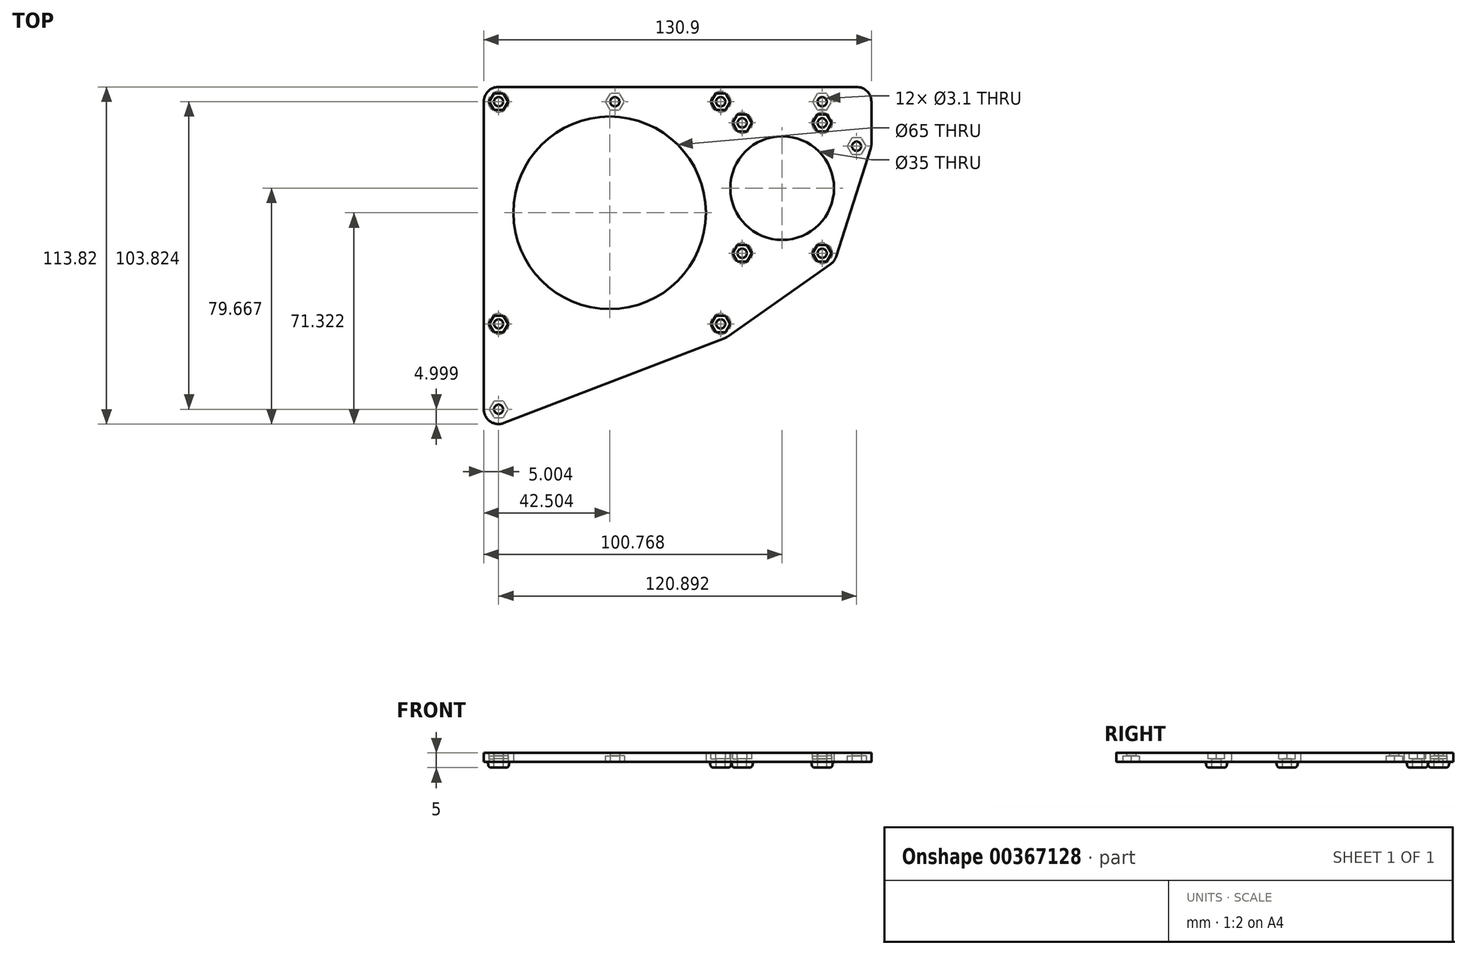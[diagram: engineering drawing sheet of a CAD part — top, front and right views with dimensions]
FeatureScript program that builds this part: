
annotation { "Feature Type Name" : "Feature", "Feature Type Description" : "" }
export const myFeature = defineFeature(function(context is Context, id is Id, definition is map)
    precondition{}
    {
        {
            var Q0;
            Q0=qCreatedBy(makeId("Top.planeOp"),FACE);
            var sketch = newSketch(context, id + "F0", { "sketchPlane" : qUnion([Q0])});
            skPoint(sketch, "E0", {"position": v(-62.97, -47.23) * mm});
            skPoint(sketch, "E1", {"position": v(-23.7, 56.6) * mm});
            skPoint(sketch, "E2", {"position": v(57.93, 41.57) * mm});
            skPoint(sketch, "E3", {"position": v(46.3, 56.6) * mm});
            skLineSegment(sketch, "E4", {"start": v(-62.97, 61.6) * mm, "end": v(57.93, 61.6) * mm});
            skLineSegment(sketch, "E5", {"start": v(62.93, 56.6) * mm, "end": v(62.93, 42.35) * mm});
            skLineSegment(sketch, "E6", {"start": v(-67.97, 56.6) * mm, "end": v(-67.97, -47.23) * mm});
            skPoint(sketch, "E7.visualSharp", {"position": v(-67.97, 61.6) * mm});
            skArc(sketch, "E7.filletArc", {"start": v(-62.97, 61.6) * mm, "mid": v(-66.5, 60.13) * mm, "end": v(-67.97, 56.6) * mm});
            skPoint(sketch, "E8.visualSharp", {"position": v(62.93, 61.6) * mm});
            skArc(sketch, "E8.filletArc", {"start": v(62.93, 56.6) * mm, "mid": v(61.46, 60.13) * mm, "end": v(57.93, 61.6) * mm});
            skLineSegment(sketch, "E9", {"start": v(-61.17, -51.9) * mm, "end": v(13.25, -23.3) * mm});
            skPoint(sketch, "E10.visualSharp", {"position": v(-67.97, -54.5) * mm});
            skArc(sketch, "E10.filletArc", {"start": v(-67.97, -47.23) * mm, "mid": v(-65.8, -51.35) * mm, "end": v(-61.17, -51.9) * mm});
            skCircle(sketch, "E11", {"center": v(-23.7, 56.6) * mm, "radius": 1.55 * mm});
            skCircle(sketch, "E12", {"center": v(46.3, 56.6) * mm, "radius": 1.55 * mm});
            skCircle(sketch, "E13", {"center": v(57.93, 41.57) * mm, "radius": 1.55 * mm});
            skCircle(sketch, "E14", {"center": v(-62.97, -47.23) * mm, "radius": 1.55 * mm});
            skPoint(sketch, "E15", {"position": v(-62.97, -18.4) * mm});
            skPoint(sketch, "E16", {"position": v(12.03, -18.4) * mm});
            skPoint(sketch, "E17", {"position": v(12.03, 56.6) * mm});
            skLineSegment(sketch, "E18", {"start": v(14.33, -22.72) * mm, "end": v(49.08, 1.7) * mm});
            skLineSegment(sketch, "E19", {"start": v(50.97, 4.26) * mm, "end": v(62.69, 40.82) * mm});
            skPoint(sketch, "E20.visualSharp", {"position": v(13.83, -23.07) * mm});
            skArc(sketch, "E20.filletArc", {"start": v(13.25, -23.3) * mm, "mid": v(13.81, -23.04) * mm, "end": v(14.33, -22.72) * mm});
            skPoint(sketch, "E21.visualSharp", {"position": v(50.45, 2.66) * mm});
            skArc(sketch, "E21.filletArc", {"start": v(49.08, 1.7) * mm, "mid": v(50.23, 2.82) * mm, "end": v(50.97, 4.26) * mm});
            skPoint(sketch, "E22.visualSharp", {"position": v(62.93, 41.57) * mm});
            skArc(sketch, "E22.filletArc", {"start": v(62.69, 40.82) * mm, "mid": v(62.87, 41.58) * mm, "end": v(62.93, 42.35) * mm});
            skCircle(sketch, "E23", {"center": v(-25.47, 19.1) * mm, "radius": 32.5 * mm});
            skCircle(sketch, "E24", {"center": v(32.8, 27.44) * mm, "radius": 17.5 * mm});
            skSolve(sketch);
        }
        {
            var Q0;
            Q0 = qSketchRegion(id + "F0", true);
            extrude(context, id + "F1", {"entities" : qUnion([Q0]), "depth" : 3 * mm});
        }
        {
            var Q0;
            Q0=makeQuery(id+"F1.opExtrude","CAP_FACE",FACE,{"disambiguationData":[OSD([sQuery(id+"F0.wireOp",EDGE,"E4"),sQuery(id+"F0.wireOp",EDGE,"E5"),sQuery(id+"F0.wireOp",EDGE,"E6"),sQuery(id+"F0.wireOp",EDGE,"E7.filletArc"),sQuery(id+"F0.wireOp",EDGE,"E8.filletArc"),sQuery(id+"F0.wireOp",EDGE,"E9"),sQuery(id+"F0.wireOp",EDGE,"E10.filletArc"),sQuery(id+"F0.wireOp",EDGE,"E11"),sQuery(id+"F0.wireOp",EDGE,"E12"),sQuery(id+"F0.wireOp",EDGE,"E13"),sQuery(id+"F0.wireOp",EDGE,"E14"),sQuery(id+"F0.wireOp",EDGE,"3iqOtTMA-anOT-yVLx-PU8o-5jLECJgI6dqX"),sQuery(id+"F0.wireOp",EDGE,"BCNSl7sb-u8Cd-CB3F-m4iC-k0AuNhckmgcP"),sQuery(id+"F0.wireOp",EDGE,"x013dWVY-SFpm-b2xf-Wu3Y-pzxELiTowayZ"),sQuery(id+"F0.wireOp",EDGE,"55sCV5fa-8bwC-iTug-WRGd-9ZglUy7d3ctR"),sQuery(id+"F0.wireOp",EDGE,"oBcL9d6C-dH0b-2MJT-6C1Z-t7KZ7XvMohC9"),sQuery(id+"F0.wireOp",EDGE,"RZnh0CVM-68zk-hnGV-QQ8E-s1oXcyv0vziq"),sQuery(id+"F0.wireOp",EDGE,"Qa9MB1tP-fu0o-2K5R-BxK5-NvYiNsFd8RXy"),sQuery(id+"F0.wireOp",EDGE,"x94zslIp-uOcx-sNJ6-LfjM-YSn8ByS7faG5"),sQuery(id+"F0.wireOp",EDGE,"E18"),sQuery(id+"F0.wireOp",EDGE,"E19"),sQuery(id+"F0.wireOp",EDGE,"E20.filletArc"),sQuery(id+"F0.wireOp",EDGE,"E21.filletArc"),sQuery(id+"F0.wireOp",EDGE,"E22.filletArc"),sQuery(id+"F0.wireOp",EDGE,"E23"),sQuery(id+"F0.wireOp",EDGE,"E24")])],"isStart":true});
            var sketch = newSketch(context, id + "F2", { "sketchPlane" : qUnion([Q0])});
            skCircle(sketch, "E25", {"center": v(-62.97, -56.6) * mm, "radius": 3.5 * mm});
            skCircle(sketch, "E26", {"center": v(12.03, -56.6) * mm, "radius": 3.5 * mm});
            skCircle(sketch, "E27", {"center": v(12.03, 18.4) * mm, "radius": 3.5 * mm});
            skCircle(sketch, "E28", {"center": v(-62.97, 18.4) * mm, "radius": 3.5 * mm});
            skCircle(sketch, "E29", {"center": v(19.3, -49.44) * mm, "radius": 3.5 * mm});
            skCircle(sketch, "E30", {"center": v(46.3, -49.44) * mm, "radius": 3.5 * mm});
            skCircle(sketch, "E31", {"center": v(46.3, -5.44) * mm, "radius": 3.5 * mm});
            skCircle(sketch, "E32", {"center": v(19.3, -5.44) * mm, "radius": 3.5 * mm});
            skSolve(sketch);
        }
        {
            var Q0;
            Q0 = qSketchRegion(id + "F2", true);
            extrude(context, id + "F3", {"entities" : qUnion([Q0]), "operationType" : NewBodyOperationType.ADD, "depth" : 2 * mm});
        }
        {
            var Q0;
            Q0=makeQuery(id+"F3.opExtrude","SWEPT_FACE",FACE,{"disambiguationData":[OSD([sQuery(id+"F2.wireOp",EDGE,"E28")])]});
            var Q1;
            Q1=makeQuery(id+"F3.opExtrude","SWEPT_FACE",FACE,{"disambiguationData":[OSD([sQuery(id+"F2.wireOp",EDGE,"E25")])]});
            var Q2;
            Q2=makeQuery(id+"F3.opExtrude","SWEPT_FACE",FACE,{"disambiguationData":[OSD([sQuery(id+"F2.wireOp",EDGE,"E27")])]});
            var Q3;
            Q3=makeQuery(id+"F3.opExtrude","SWEPT_FACE",FACE,{"disambiguationData":[OSD([sQuery(id+"F2.wireOp",EDGE,"E32")])]});
            var Q4;
            Q4=makeQuery(id+"F3.opExtrude","SWEPT_FACE",FACE,{"disambiguationData":[OSD([sQuery(id+"F2.wireOp",EDGE,"E29")])]});
            var Q5;
            Q5=makeQuery(id+"F3.opExtrude","SWEPT_FACE",FACE,{"disambiguationData":[OSD([sQuery(id+"F2.wireOp",EDGE,"E26")])]});
            var Q6;
            Q6=makeQuery(id+"F3.opExtrude","SWEPT_FACE",FACE,{"disambiguationData":[OSD([sQuery(id+"F2.wireOp",EDGE,"E31")])]});
            var Q7;
            Q7=makeQuery(id+"F3.opExtrude","SWEPT_FACE",FACE,{"disambiguationData":[OSD([sQuery(id+"F2.wireOp",EDGE,"E30")])]});
            fillet(context, id + "F4", {"entities" : qUnion([Q0, Q1, Q2, Q3, Q4, Q5, Q6, Q7]), "radius" : 1 * mm, "tangentPropagation" : true, "allowEdgeOverflow" : false});
        }
        {
            var Q0;
            Q0=makeQuery(id+"F1.opExtrude","CAP_FACE",FACE,{"disambiguationData":[OSD([sQuery(id+"F0.wireOp",EDGE,"E4"),sQuery(id+"F0.wireOp",EDGE,"E5"),sQuery(id+"F0.wireOp",EDGE,"E6"),sQuery(id+"F0.wireOp",EDGE,"E7.filletArc"),sQuery(id+"F0.wireOp",EDGE,"E8.filletArc"),sQuery(id+"F0.wireOp",EDGE,"E9"),sQuery(id+"F0.wireOp",EDGE,"E10.filletArc"),sQuery(id+"F0.wireOp",EDGE,"E11"),sQuery(id+"F0.wireOp",EDGE,"E12"),sQuery(id+"F0.wireOp",EDGE,"E13"),sQuery(id+"F0.wireOp",EDGE,"E14"),sQuery(id+"F0.wireOp",EDGE,"3iqOtTMA-anOT-yVLx-PU8o-5jLECJgI6dqX"),sQuery(id+"F0.wireOp",EDGE,"BCNSl7sb-u8Cd-CB3F-m4iC-k0AuNhckmgcP"),sQuery(id+"F0.wireOp",EDGE,"x013dWVY-SFpm-b2xf-Wu3Y-pzxELiTowayZ"),sQuery(id+"F0.wireOp",EDGE,"55sCV5fa-8bwC-iTug-WRGd-9ZglUy7d3ctR"),sQuery(id+"F0.wireOp",EDGE,"oBcL9d6C-dH0b-2MJT-6C1Z-t7KZ7XvMohC9"),sQuery(id+"F0.wireOp",EDGE,"RZnh0CVM-68zk-hnGV-QQ8E-s1oXcyv0vziq"),sQuery(id+"F0.wireOp",EDGE,"Qa9MB1tP-fu0o-2K5R-BxK5-NvYiNsFd8RXy"),sQuery(id+"F0.wireOp",EDGE,"x94zslIp-uOcx-sNJ6-LfjM-YSn8ByS7faG5"),sQuery(id+"F0.wireOp",EDGE,"E18"),sQuery(id+"F0.wireOp",EDGE,"E19"),sQuery(id+"F0.wireOp",EDGE,"E20.filletArc"),sQuery(id+"F0.wireOp",EDGE,"E21.filletArc"),sQuery(id+"F0.wireOp",EDGE,"E22.filletArc"),sQuery(id+"F0.wireOp",EDGE,"E23"),sQuery(id+"F0.wireOp",EDGE,"E24")])],"isStart":false});
            var sketch = newSketch(context, id + "F5", { "sketchPlane" : qUnion([Q0])});
            skCircle(sketch, "E33.cCircle", {"center": v(-62.97, -18.4) * mm, "radius": 2.8 * mm, "construction": true});
            skLineSegment(sketch, "E33.0", {"start": v(-61.35, -21.2) * mm, "end": v(-64.58, -21.2) * mm});
            skLineSegment(sketch, "E33.1", {"start": v(-64.58, -21.2) * mm, "end": v(-66.2, -18.4) * mm});
            skLineSegment(sketch, "E33.2", {"start": v(-66.2, -18.4) * mm, "end": v(-64.58, -15.6) * mm});
            skLineSegment(sketch, "E33.3", {"start": v(-64.58, -15.6) * mm, "end": v(-61.35, -15.6) * mm});
            skLineSegment(sketch, "E33.4", {"start": v(-61.35, -15.6) * mm, "end": v(-59.73, -18.4) * mm});
            skLineSegment(sketch, "E33.5", {"start": v(-59.73, -18.4) * mm, "end": v(-61.35, -21.2) * mm});
            skPoint(sketch, "E33.0.midPoint", {"position": v(-62.97, -21.2) * mm});
            skCircle(sketch, "E34.cCircle", {"center": v(12.03, -18.4) * mm, "radius": 2.8 * mm, "construction": true});
            skLineSegment(sketch, "E34.0", {"start": v(13.65, -21.2) * mm, "end": v(10.42, -21.2) * mm});
            skLineSegment(sketch, "E34.1", {"start": v(10.42, -21.2) * mm, "end": v(8.8, -18.4) * mm});
            skLineSegment(sketch, "E34.2", {"start": v(8.8, -18.4) * mm, "end": v(10.42, -15.6) * mm});
            skLineSegment(sketch, "E34.3", {"start": v(10.42, -15.6) * mm, "end": v(13.65, -15.6) * mm});
            skLineSegment(sketch, "E34.4", {"start": v(13.65, -15.6) * mm, "end": v(15.27, -18.4) * mm});
            skLineSegment(sketch, "E34.5", {"start": v(15.27, -18.4) * mm, "end": v(13.65, -21.2) * mm});
            skPoint(sketch, "E34.0.midPoint", {"position": v(12.03, -21.2) * mm});
            skCircle(sketch, "E35.cCircle", {"center": v(19.3, 5.44) * mm, "radius": 2.8 * mm, "construction": true});
            skLineSegment(sketch, "E35.0", {"start": v(20.91, 2.64) * mm, "end": v(17.68, 2.64) * mm});
            skLineSegment(sketch, "E35.1", {"start": v(17.68, 2.64) * mm, "end": v(16.06, 5.44) * mm});
            skLineSegment(sketch, "E35.2", {"start": v(16.06, 5.44) * mm, "end": v(17.68, 8.24) * mm});
            skLineSegment(sketch, "E35.3", {"start": v(17.68, 8.24) * mm, "end": v(20.91, 8.24) * mm});
            skLineSegment(sketch, "E35.4", {"start": v(20.91, 8.24) * mm, "end": v(22.53, 5.44) * mm});
            skLineSegment(sketch, "E35.5", {"start": v(22.53, 5.44) * mm, "end": v(20.91, 2.64) * mm});
            skPoint(sketch, "E35.0.midPoint", {"position": v(19.3, 2.64) * mm});
            skCircle(sketch, "E36.cCircle", {"center": v(-62.97, 56.6) * mm, "radius": 2.8 * mm, "construction": true});
            skLineSegment(sketch, "E36.0", {"start": v(-61.35, 53.8) * mm, "end": v(-64.58, 53.8) * mm});
            skLineSegment(sketch, "E36.1", {"start": v(-64.58, 53.8) * mm, "end": v(-66.2, 56.6) * mm});
            skLineSegment(sketch, "E36.2", {"start": v(-66.2, 56.6) * mm, "end": v(-64.58, 59.4) * mm});
            skLineSegment(sketch, "E36.3", {"start": v(-64.58, 59.4) * mm, "end": v(-61.35, 59.4) * mm});
            skLineSegment(sketch, "E36.4", {"start": v(-61.35, 59.4) * mm, "end": v(-59.73, 56.6) * mm});
            skLineSegment(sketch, "E36.5", {"start": v(-59.73, 56.6) * mm, "end": v(-61.35, 53.8) * mm});
            skPoint(sketch, "E36.0.midPoint", {"position": v(-62.97, 53.8) * mm});
            skCircle(sketch, "E37.cCircle", {"center": v(12.03, 56.6) * mm, "radius": 2.8 * mm, "construction": true});
            skLineSegment(sketch, "E37.0", {"start": v(13.65, 53.8) * mm, "end": v(10.42, 53.8) * mm});
            skLineSegment(sketch, "E37.1", {"start": v(10.42, 53.8) * mm, "end": v(8.8, 56.6) * mm});
            skLineSegment(sketch, "E37.2", {"start": v(8.8, 56.6) * mm, "end": v(10.42, 59.4) * mm});
            skLineSegment(sketch, "E37.3", {"start": v(10.42, 59.4) * mm, "end": v(13.65, 59.4) * mm});
            skLineSegment(sketch, "E37.4", {"start": v(13.65, 59.4) * mm, "end": v(15.27, 56.6) * mm});
            skLineSegment(sketch, "E37.5", {"start": v(15.27, 56.6) * mm, "end": v(13.65, 53.8) * mm});
            skPoint(sketch, "E37.0.midPoint", {"position": v(12.03, 53.8) * mm});
            skCircle(sketch, "E38.cCircle", {"center": v(19.3, 49.44) * mm, "radius": 2.8 * mm, "construction": true});
            skLineSegment(sketch, "E38.0", {"start": v(20.91, 46.64) * mm, "end": v(17.68, 46.64) * mm});
            skLineSegment(sketch, "E38.1", {"start": v(17.68, 46.64) * mm, "end": v(16.06, 49.44) * mm});
            skLineSegment(sketch, "E38.2", {"start": v(16.06, 49.44) * mm, "end": v(17.68, 52.24) * mm});
            skLineSegment(sketch, "E38.3", {"start": v(17.68, 52.24) * mm, "end": v(20.91, 52.24) * mm});
            skLineSegment(sketch, "E38.4", {"start": v(20.91, 52.24) * mm, "end": v(22.53, 49.44) * mm});
            skLineSegment(sketch, "E38.5", {"start": v(22.53, 49.44) * mm, "end": v(20.91, 46.64) * mm});
            skPoint(sketch, "E38.0.midPoint", {"position": v(19.3, 46.64) * mm});
            skCircle(sketch, "E39.cCircle", {"center": v(46.3, 49.44) * mm, "radius": 2.8 * mm, "construction": true});
            skLineSegment(sketch, "E39.0", {"start": v(47.91, 46.64) * mm, "end": v(44.68, 46.64) * mm});
            skLineSegment(sketch, "E39.1", {"start": v(44.68, 46.64) * mm, "end": v(43.06, 49.44) * mm});
            skLineSegment(sketch, "E39.2", {"start": v(43.06, 49.44) * mm, "end": v(44.68, 52.24) * mm});
            skLineSegment(sketch, "E39.3", {"start": v(44.68, 52.24) * mm, "end": v(47.91, 52.24) * mm});
            skLineSegment(sketch, "E39.4", {"start": v(47.91, 52.24) * mm, "end": v(49.53, 49.44) * mm});
            skLineSegment(sketch, "E39.5", {"start": v(49.53, 49.44) * mm, "end": v(47.91, 46.64) * mm});
            skPoint(sketch, "E39.0.midPoint", {"position": v(46.3, 46.64) * mm});
            skCircle(sketch, "E40.cCircle", {"center": v(46.3, 5.44) * mm, "radius": 2.8 * mm, "construction": true});
            skLineSegment(sketch, "E40.0", {"start": v(44.68, 8.24) * mm, "end": v(47.91, 8.24) * mm});
            skLineSegment(sketch, "E40.1", {"start": v(47.91, 8.24) * mm, "end": v(49.53, 5.44) * mm});
            skLineSegment(sketch, "E40.2", {"start": v(49.53, 5.44) * mm, "end": v(47.91, 2.64) * mm});
            skLineSegment(sketch, "E40.3", {"start": v(47.91, 2.64) * mm, "end": v(44.68, 2.64) * mm});
            skLineSegment(sketch, "E40.4", {"start": v(44.68, 2.64) * mm, "end": v(43.06, 5.44) * mm});
            skLineSegment(sketch, "E40.5", {"start": v(43.06, 5.44) * mm, "end": v(44.68, 8.24) * mm});
            skPoint(sketch, "E40.0.midPoint", {"position": v(46.3, 8.24) * mm});
            skSolve(sketch);
        }
        {
            var Q0;
            Q0 = qSketchRegion(id + "F5", true);
            extrude(context, id + "F6", {"entities" : qUnion([Q0]), "operationType" : NewBodyOperationType.REMOVE, "oppositeDirection" : true, "depth" : 2 * mm});
        }
        {
            var Q0;
            Q0=makeQuery(id+"F1.opExtrude","CAP_FACE",FACE,{"disambiguationData":[OSD([sQuery(id+"F0.wireOp",EDGE,"E4"),sQuery(id+"F0.wireOp",EDGE,"E5"),sQuery(id+"F0.wireOp",EDGE,"E6"),sQuery(id+"F0.wireOp",EDGE,"E7.filletArc"),sQuery(id+"F0.wireOp",EDGE,"E8.filletArc"),sQuery(id+"F0.wireOp",EDGE,"E9"),sQuery(id+"F0.wireOp",EDGE,"E10.filletArc"),sQuery(id+"F0.wireOp",EDGE,"E11"),sQuery(id+"F0.wireOp",EDGE,"E12"),sQuery(id+"F0.wireOp",EDGE,"E13"),sQuery(id+"F0.wireOp",EDGE,"E14"),sQuery(id+"F0.wireOp",EDGE,"E18"),sQuery(id+"F0.wireOp",EDGE,"E19"),sQuery(id+"F0.wireOp",EDGE,"E20.filletArc"),sQuery(id+"F0.wireOp",EDGE,"E21.filletArc"),sQuery(id+"F0.wireOp",EDGE,"E22.filletArc"),sQuery(id+"F0.wireOp",EDGE,"E23"),sQuery(id+"F0.wireOp",EDGE,"E24")])],"isStart":false});
            var sketch = newSketch(context, id + "F7", { "sketchPlane" : qUnion([Q0])});
            skCircle(sketch, "E41", {"center": v(-62.97, 56.6) * mm, "radius": 1.55 * mm});
            skCircle(sketch, "E42", {"center": v(-62.97, -18.4) * mm, "radius": 1.55 * mm});
            skCircle(sketch, "E43", {"center": v(19.3, 5.44) * mm, "radius": 1.55 * mm});
            skCircle(sketch, "E44", {"center": v(46.3, 5.44) * mm, "radius": 1.55 * mm});
            skCircle(sketch, "E45", {"center": v(46.3, 49.44) * mm, "radius": 1.55 * mm});
            skCircle(sketch, "E46", {"center": v(19.3, 49.44) * mm, "radius": 1.55 * mm});
            skCircle(sketch, "E47", {"center": v(12.03, -18.4) * mm, "radius": 1.55 * mm});
            skCircle(sketch, "E48", {"center": v(12.03, 56.6) * mm, "radius": 1.55 * mm});
            skSolve(sketch);
        }
        {
            var Q0;
            Q0 = qSketchRegion(id + "F7", true);
            extrude(context, id + "F8", {"entities" : qUnion([Q0]), "operationType" : NewBodyOperationType.REMOVE, "oppositeDirection" : true, "depth" : 25 * mm});
        }
        {
            var Q0;
            Q0=makeQuery(id+"F1.opExtrude","CAP_FACE",FACE,{"disambiguationData":[OSD([sQuery(id+"F0.wireOp",EDGE,"E4"),sQuery(id+"F0.wireOp",EDGE,"E5"),sQuery(id+"F0.wireOp",EDGE,"E6"),sQuery(id+"F0.wireOp",EDGE,"E7.filletArc"),sQuery(id+"F0.wireOp",EDGE,"E8.filletArc"),sQuery(id+"F0.wireOp",EDGE,"E9"),sQuery(id+"F0.wireOp",EDGE,"E10.filletArc"),sQuery(id+"F0.wireOp",EDGE,"E11"),sQuery(id+"F0.wireOp",EDGE,"E12"),sQuery(id+"F0.wireOp",EDGE,"E13"),sQuery(id+"F0.wireOp",EDGE,"E14"),sQuery(id+"F0.wireOp",EDGE,"E18"),sQuery(id+"F0.wireOp",EDGE,"E19"),sQuery(id+"F0.wireOp",EDGE,"E20.filletArc"),sQuery(id+"F0.wireOp",EDGE,"E21.filletArc"),sQuery(id+"F0.wireOp",EDGE,"E22.filletArc"),sQuery(id+"F0.wireOp",EDGE,"E23"),sQuery(id+"F0.wireOp",EDGE,"E24")])],"isStart":true});
            var sketch = newSketch(context, id + "F9", { "sketchPlane" : qUnion([Q0])});
            skCircle(sketch, "E49.cCircle", {"center": v(-62.97, 47.23) * mm, "radius": 2.8 * mm, "construction": true});
            skLineSegment(sketch, "E49.0", {"start": v(-61.35, 44.43) * mm, "end": v(-64.58, 44.43) * mm});
            skLineSegment(sketch, "E49.1", {"start": v(-64.58, 44.43) * mm, "end": v(-66.2, 47.23) * mm});
            skLineSegment(sketch, "E49.2", {"start": v(-66.2, 47.23) * mm, "end": v(-64.58, 50.03) * mm});
            skLineSegment(sketch, "E49.3", {"start": v(-64.58, 50.03) * mm, "end": v(-61.35, 50.03) * mm});
            skLineSegment(sketch, "E49.4", {"start": v(-61.35, 50.03) * mm, "end": v(-59.73, 47.23) * mm});
            skLineSegment(sketch, "E49.5", {"start": v(-59.73, 47.23) * mm, "end": v(-61.35, 44.43) * mm});
            skPoint(sketch, "E49.0.midPoint", {"position": v(-62.97, 44.43) * mm});
            skCircle(sketch, "E50.cCircle", {"center": v(-23.7, -56.6) * mm, "radius": 2.8 * mm, "construction": true});
            skLineSegment(sketch, "E50.0", {"start": v(-22.09, -59.4) * mm, "end": v(-25.32, -59.4) * mm});
            skLineSegment(sketch, "E50.1", {"start": v(-25.32, -59.4) * mm, "end": v(-26.94, -56.6) * mm});
            skLineSegment(sketch, "E50.2", {"start": v(-26.94, -56.6) * mm, "end": v(-25.32, -53.8) * mm});
            skLineSegment(sketch, "E50.3", {"start": v(-25.32, -53.8) * mm, "end": v(-22.09, -53.8) * mm});
            skLineSegment(sketch, "E50.4", {"start": v(-22.09, -53.8) * mm, "end": v(-20.47, -56.6) * mm});
            skLineSegment(sketch, "E50.5", {"start": v(-20.47, -56.6) * mm, "end": v(-22.09, -59.4) * mm});
            skPoint(sketch, "E50.0.midPoint", {"position": v(-23.7, -59.4) * mm});
            skCircle(sketch, "E51.cCircle", {"center": v(46.3, -56.6) * mm, "radius": 2.8 * mm, "construction": true});
            skLineSegment(sketch, "E51.0", {"start": v(47.91, -59.4) * mm, "end": v(44.68, -59.4) * mm});
            skLineSegment(sketch, "E51.1", {"start": v(44.68, -59.4) * mm, "end": v(43.06, -56.6) * mm});
            skLineSegment(sketch, "E51.2", {"start": v(43.06, -56.6) * mm, "end": v(44.68, -53.8) * mm});
            skLineSegment(sketch, "E51.3", {"start": v(44.68, -53.8) * mm, "end": v(47.91, -53.8) * mm});
            skLineSegment(sketch, "E51.4", {"start": v(47.91, -53.8) * mm, "end": v(49.53, -56.6) * mm});
            skLineSegment(sketch, "E51.5", {"start": v(49.53, -56.6) * mm, "end": v(47.91, -59.4) * mm});
            skPoint(sketch, "E51.0.midPoint", {"position": v(46.3, -59.4) * mm});
            skCircle(sketch, "E52.cCircle", {"center": v(57.93, -41.57) * mm, "radius": 2.8 * mm, "construction": true});
            skLineSegment(sketch, "E52.0", {"start": v(59.54, -44.37) * mm, "end": v(56.3, -44.37) * mm});
            skLineSegment(sketch, "E52.1", {"start": v(56.3, -44.37) * mm, "end": v(54.7, -41.57) * mm});
            skLineSegment(sketch, "E52.2", {"start": v(54.7, -41.57) * mm, "end": v(56.3, -38.77) * mm});
            skLineSegment(sketch, "E52.3", {"start": v(56.3, -38.77) * mm, "end": v(59.54, -38.77) * mm});
            skLineSegment(sketch, "E52.4", {"start": v(59.54, -38.77) * mm, "end": v(61.16, -41.57) * mm});
            skLineSegment(sketch, "E52.5", {"start": v(61.16, -41.57) * mm, "end": v(59.54, -44.37) * mm});
            skPoint(sketch, "E52.0.midPoint", {"position": v(57.93, -44.37) * mm});
            skSolve(sketch);
        }
        {
            var Q0;
            Q0 = qSketchRegion(id + "F9", true);
            extrude(context, id + "F10", {"entities" : qUnion([Q0]), "operationType" : NewBodyOperationType.REMOVE, "oppositeDirection" : true, "depth" : 2 * mm});
        }
    });
